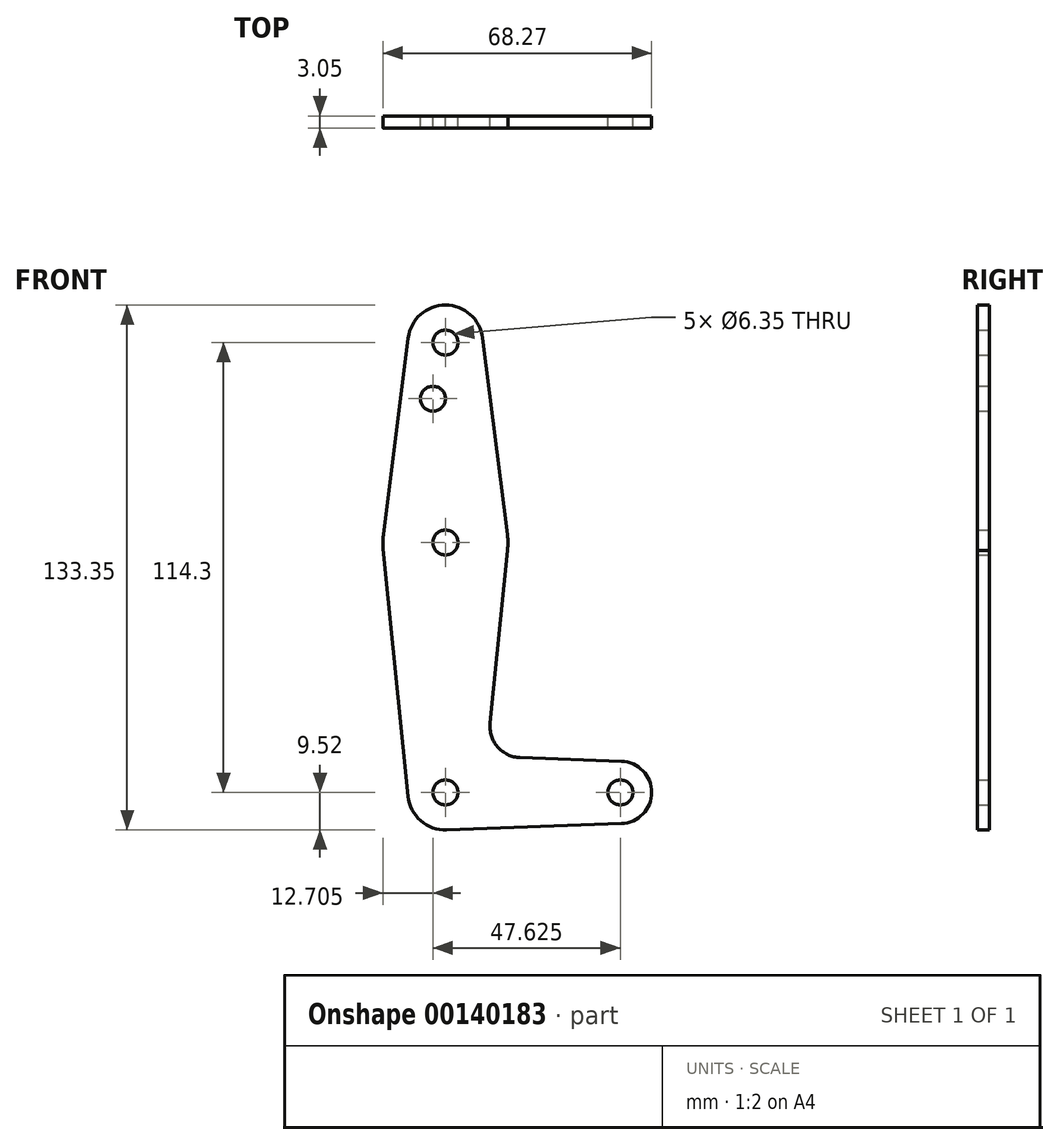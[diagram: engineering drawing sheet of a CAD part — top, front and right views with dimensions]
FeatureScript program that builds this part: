
annotation { "Feature Type Name" : "Feature", "Feature Type Description" : "" }
export const myFeature = defineFeature(function(context is Context, id is Id, definition is map)
    precondition{}
    {
        {
            var Q0;
            Q0=qCreatedBy(makeId("Front.planeOp"),FACE);
            var sketch = newSketch(context, id + "F0", { "sketchPlane" : qUnion([Q0])});
            skLineSegment(sketch, "E0", {"start": v(0, 114.3) * mm, "end": v(0, 0) * mm, "construction": true});
            skLineSegment(sketch, "E1", {"start": v(0, 0) * mm, "end": v(44.45, 0) * mm, "construction": true});
            skCircle(sketch, "E2", {"center": v(0, 114.3) * mm, "radius": 9.53 * mm});
            skCircle(sketch, "E3", {"center": v(0, 63.5) * mm, "radius": 15.88 * mm});
            skCircle(sketch, "E4", {"center": v(0, 0) * mm, "radius": 9.52 * mm});
            skCircle(sketch, "E5", {"center": v(44.45, 0) * mm, "radius": 7.94 * mm});
            skLineSegment(sketch, "E6", {"start": v(-9.45, 115.5) * mm, "end": v(-15.75, 65.48) * mm});
            skLineSegment(sketch, "E7", {"start": v(9.45, 115.5) * mm, "end": v(15.75, 65.48) * mm});
            skLineSegment(sketch, "E8", {"start": v(-15.8, 61.91) * mm, "end": v(-9.48, -0.95) * mm});
            skLineSegment(sketch, "E9", {"start": v(15.75, 61.52) * mm, "end": v(11.34, 17.6) * mm});
            skLineSegment(sketch, "E10", {"start": v(18.97, 8.85) * mm, "end": v(44.73, 7.93) * mm});
            skLineSegment(sketch, "E11", {"start": v(0.34, -9.52) * mm, "end": v(44.73, -7.93) * mm});
            skCircle(sketch, "E12", {"center": v(0, 114.3) * mm, "radius": 3.18 * mm});
            skCircle(sketch, "E13", {"center": v(0, 63.5) * mm, "radius": 3.18 * mm});
            skCircle(sketch, "E14", {"center": v(0, 0) * mm, "radius": 3.18 * mm});
            skCircle(sketch, "E15", {"center": v(44.45, 0) * mm, "radius": 3.18 * mm});
            skCircle(sketch, "E16", {"center": v(-3.17, 100.03) * mm, "radius": 3.18 * mm});
            skArc(sketch, "E17.filletArc", {"start": v(11.34, 17.6) * mm, "mid": v(13.26, 11.57) * mm, "end": v(18.97, 8.85) * mm});
            skSolve(sketch);
        }
        {
            var Q0;
            Q0 = qSketchRegion(id + "F0", true);
            extrude(context, id + "F1", {"entities" : qUnion([Q0]), "depth" : 3.05 * mm});
        }
    });
